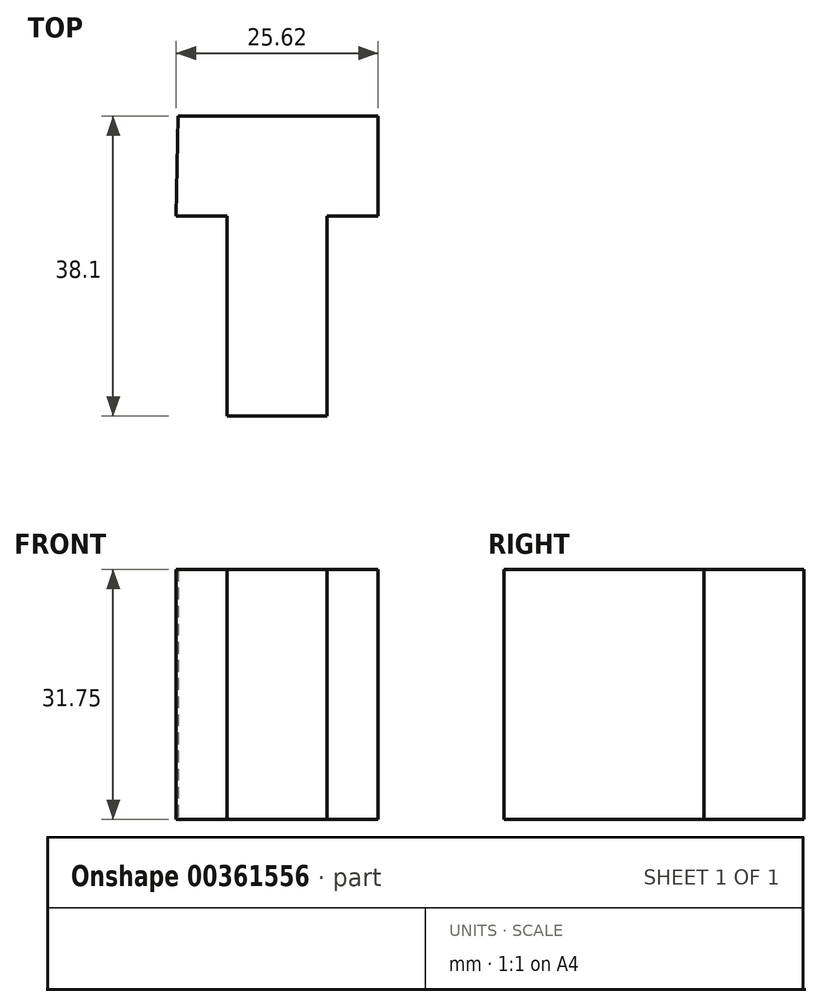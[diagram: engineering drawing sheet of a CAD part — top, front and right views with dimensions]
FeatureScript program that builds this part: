
annotation { "Feature Type Name" : "Feature", "Feature Type Description" : "" }
export const myFeature = defineFeature(function(context is Context, id is Id, definition is map)
    precondition{}
    {
        {
            var Q0;
            Q0=qCreatedBy(makeId("Top.planeOp"),FACE);
            var sketch = newSketch(context, id + "F0", { "sketchPlane" : qUnion([Q0])});
            skLineSegment(sketch, "E0", {"start": v(-13.6, 38.1) * mm, "end": v(11.8, 38.1) * mm});
            skLineSegment(sketch, "E1", {"start": v(11.8, 38.1) * mm, "end": v(11.8, 25.4) * mm});
            skLineSegment(sketch, "E2", {"start": v(11.8, 25.4) * mm, "end": v(5.33, 25.4) * mm});
            skLineSegment(sketch, "E3", {"start": v(5.33, 25.4) * mm, "end": v(5.33, 0) * mm});
            skLineSegment(sketch, "E4", {"start": v(5.33, 0) * mm, "end": v(-7.37, 0) * mm});
            skLineSegment(sketch, "E5", {"start": v(-7.37, 0) * mm, "end": v(-7.37, 25.4) * mm});
            skLineSegment(sketch, "E6", {"start": v(-7.37, 25.4) * mm, "end": v(-13.83, 25.4) * mm});
            skLineSegment(sketch, "E7", {"start": v(-13.83, 25.4) * mm, "end": v(-13.6, 38.1) * mm});
            skSolve(sketch);
        }
        {
            var Q0;
            Q0=makeQuery(id+"F0.imprint","IMPRINT",FACE,{"disambiguationData":[TD([[makeQuery(id+"F0.imprint","IMPRINT",EDGE,{"derivedFrom":sQuery(id+"F0.wireOp",EDGE,"E0")}),-1.0]])]});
            extrude(context, id + "F1", {"entities" : qUnion([Q0]), "depth" : 31.75 * mm});
        }
    });
